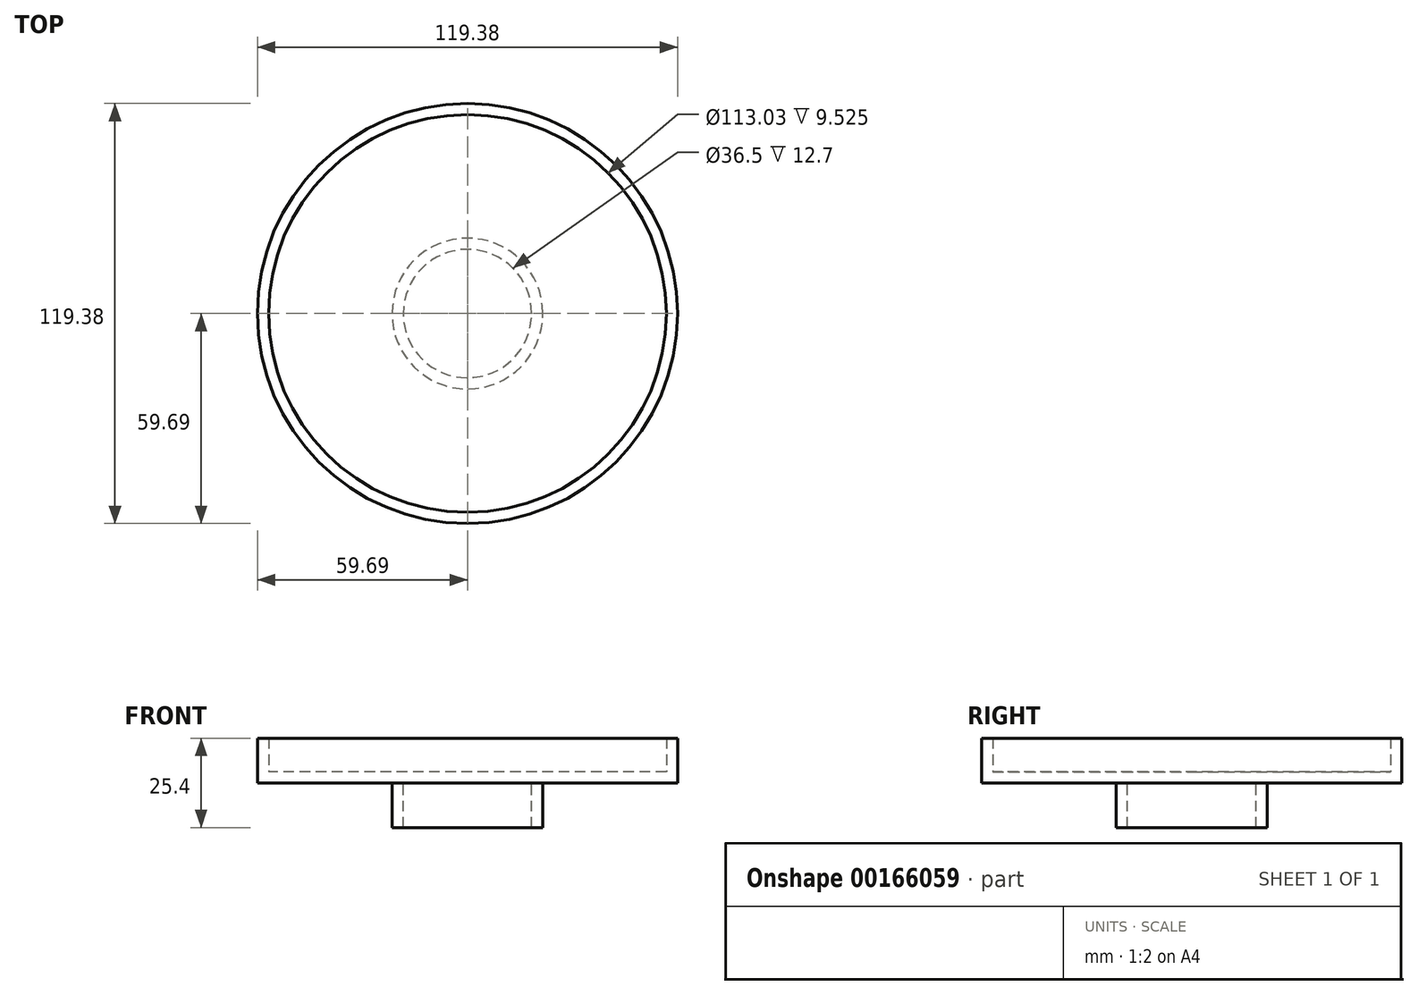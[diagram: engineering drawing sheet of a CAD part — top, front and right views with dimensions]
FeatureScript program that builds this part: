
annotation { "Feature Type Name" : "Feature", "Feature Type Description" : "" }
export const myFeature = defineFeature(function(context is Context, id is Id, definition is map)
    precondition{}
    {
        {
            var Q0;
            Q0=qCreatedBy(makeId("Top.planeOp"),FACE);
            var sketch = newSketch(context, id + "F0", { "sketchPlane" : qUnion([Q0])});
            skCircle(sketch, "E0", {"center": v(0, 0) * mm, "radius": 56.52 * mm});
            skCircle(sketch, "E1.0", {"center": v(0, 0) * mm, "radius": 59.7 * mm});
            skSolve(sketch);
        }
        {
            var Q0;
            Q0 = qSketchRegion(id + "F0", true);
            extrude(context, id + "F1", {"entities" : qUnion([Q0]), "depth" : 12.7 * mm});
        }
        {
            var Q0;
            Q0=makeQuery(id+"F0.imprint","IMPRINT",FACE,{"disambiguationData":[TD([[makeQuery(id+"F0.imprint","IMPRINT",EDGE,{"derivedFrom":sQuery(id+"F0.wireOp",EDGE,"E0")}),1.0]])]});
            extrude(context, id + "F2", {"entities" : qUnion([Q0]), "operationType" : NewBodyOperationType.ADD, "depth" : 3.17 * mm});
        }
        {
            var Q0;
            Q0=makeQuery(id+"F0.imprint","IMPRINT",FACE,{"disambiguationData":[TD([[makeQuery(id+"F0.imprint","IMPRINT",EDGE,{"derivedFrom":sQuery(id+"F0.wireOp",EDGE,"E0")}),1.0]])]});
            var sketch = newSketch(context, id + "F3", { "sketchPlane" : qUnion([Q0])});
            skCircle(sketch, "E2", {"center": v(0, 0) * mm, "radius": 18.25 * mm});
            skCircle(sketch, "E3.0", {"center": v(0, 0) * mm, "radius": 21.43 * mm});
            skSolve(sketch);
        }
        {
            var Q0;
            Q0 = qSketchRegion(id + "F3", true);
            var Q1;
            Q1=makeQuery(id+"F3.imprint","IMPRINT",FACE,{"disambiguationData":[TD([[makeQuery(id+"F3.imprint","IMPRINT",EDGE,{"derivedFrom":sQuery(id+"F3.wireOp",EDGE,"2cosm7w3-FYu5-aE3T-nJ1e-qJXA08603Gwl")}),1.0]])]});
            extrude(context, id + "F4", {"entities" : qUnion([Q0, Q1]), "operationType" : NewBodyOperationType.ADD, "oppositeDirection" : true, "depth" : 12.7 * mm});
        }
    });
